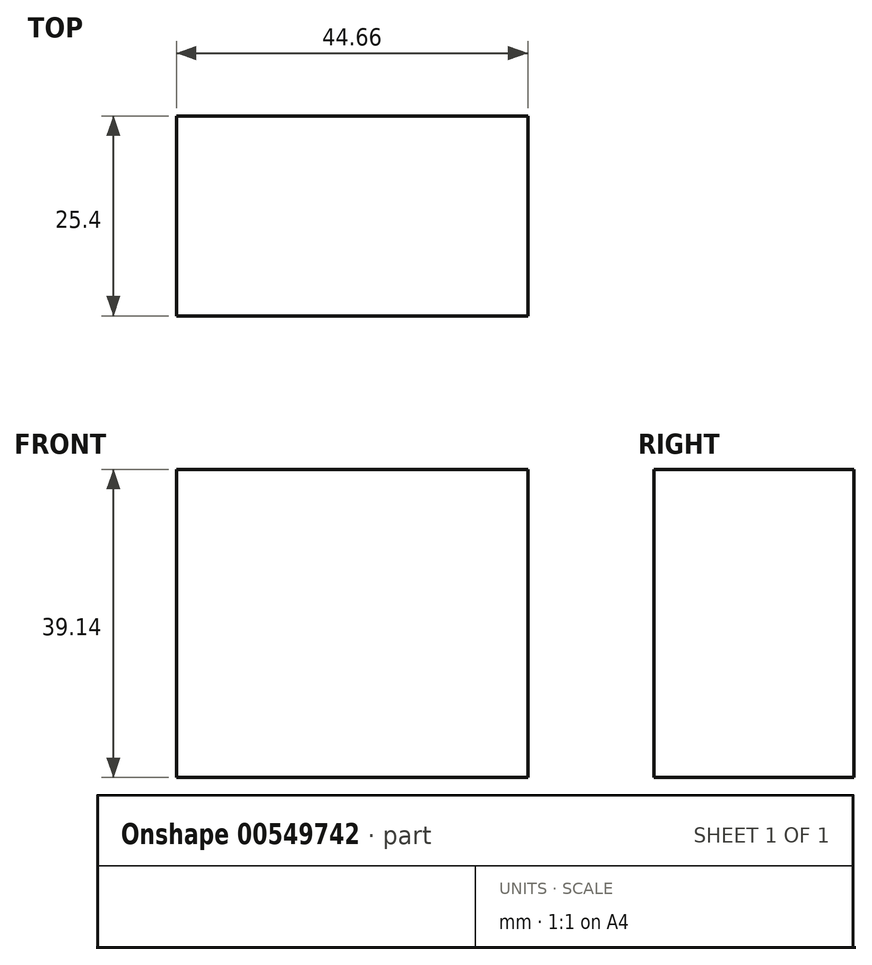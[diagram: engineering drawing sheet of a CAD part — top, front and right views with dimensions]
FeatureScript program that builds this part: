
annotation { "Feature Type Name" : "Feature", "Feature Type Description" : "" }
export const myFeature = defineFeature(function(context is Context, id is Id, definition is map)
    precondition{}
    {
        {
            var Q0;
            Q0=qCreatedBy(makeId("Front.planeOp"),FACE);
            var sketch = newSketch(context, id + "F0", { "sketchPlane" : qUnion([Q0])});
            skLineSegment(sketch, "E0.bottom", {"start": v(-104.87, 54.2) * mm, "end": v(-60.21, 54.2) * mm});
            skLineSegment(sketch, "E0.top", {"start": v(-104.87, 15.05) * mm, "end": v(-60.21, 15.05) * mm});
            skLineSegment(sketch, "E0.left", {"start": v(-104.87, 54.2) * mm, "end": v(-104.87, 15.05) * mm});
            skLineSegment(sketch, "E0.right", {"start": v(-60.21, 54.2) * mm, "end": v(-60.21, 15.05) * mm});
            skCircle(sketch, "E1", {"center": v(25.09, 26.6) * mm, "radius": 23.75 * mm});
            skSolve(sketch);
        }
        {
            var Q0;
            Q0=makeQuery(id+"F0.imprint","IMPRINT",FACE,{"disambiguationData":[TD([[makeQuery(id+"F0.imprint","IMPRINT",EDGE,{"derivedFrom":sQuery(id+"F0.wireOp",EDGE,"E0.bottom")}),-1.0]])]});
            extrude(context, id + "F1", {"entities" : qUnion([Q0]), "depth" : 25.4 * mm, "offsetDistance" : 25.4 * mm});
        }
        {
            var Q0;
            Q0=sQuery(id+"F0.wireOp",EDGE,"E1");
            extrude(context, id + "F2", {"bodyType" : ToolBodyType.SURFACE, "surfaceEntities" : qUnion([Q0]), "depth" : 25.4 * mm, "offsetDistance" : 25.4 * mm});
        }
    });
